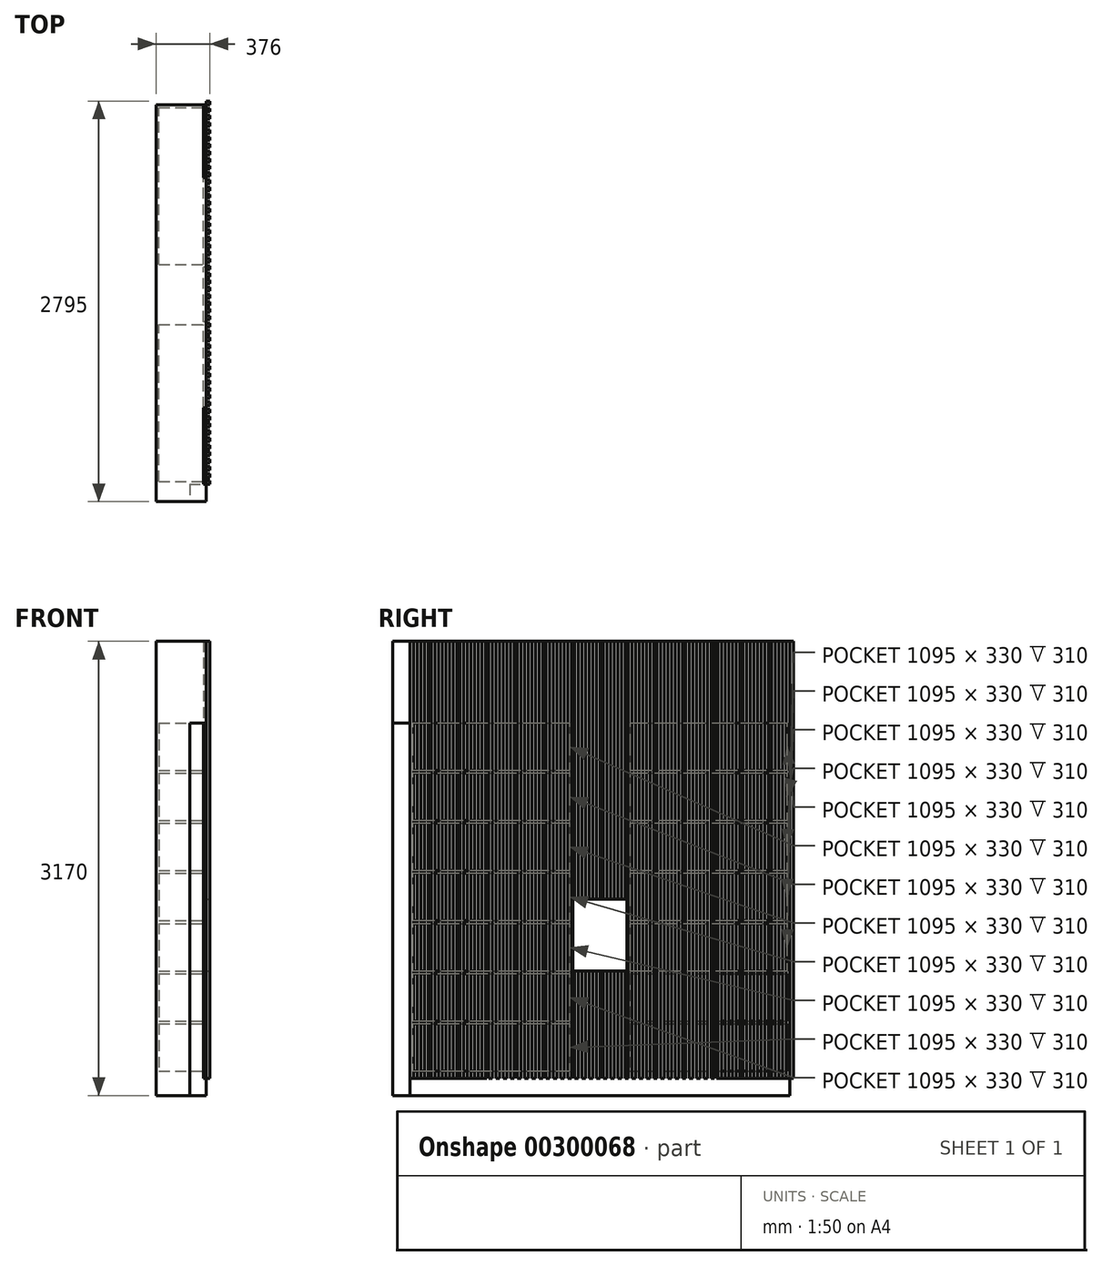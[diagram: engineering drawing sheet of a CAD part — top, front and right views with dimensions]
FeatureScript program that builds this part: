
annotation { "Feature Type Name" : "Feature", "Feature Type Description" : "" }
export const myFeature = defineFeature(function(context is Context, id is Id, definition is map)
    precondition{}
    {
        {
            var Q0;
            Q0=qCreatedBy(makeId("Top.planeOp"),FACE);
            var sketch = newSketch(context, id + "F0", { "sketchPlane" : qUnion([Q0])});
            skLineSegment(sketch, "E0.bottom", {"start": v(0, 0) * mm, "end": v(350, 0) * mm});
            skLineSegment(sketch, "E0.top", {"start": v(0, 2650) * mm, "end": v(350, 2650) * mm});
            skLineSegment(sketch, "E0.left", {"start": v(0, 0) * mm, "end": v(0, 2650) * mm});
            skLineSegment(sketch, "E0.right", {"start": v(350, 0) * mm, "end": v(350, 2650) * mm});
            skLineSegment(sketch, "E1", {"start": v(0, 2770) * mm, "end": v(350, 2770) * mm, "construction": true});
            skSolve(sketch);
        }
        {
            var Q0;
            Q0=qCreatedBy(makeId("Top.planeOp"),FACE);
            cPlane(context, id + "F1", {"entities" : qUnion([Q0]), "cplaneType" : CPlaneType.OFFSET, "offset" : 120 * mm, "width" : 150 * mm, "height" : 150 * mm});
        }
        {
            var Q0;
            Q0=makeQuery(id+"F0.imprint","IMPRINT",FACE,{"disambiguationData":[TD([[makeQuery(id+"F0.imprint","IMPRINT",EDGE,{"derivedFrom":sQuery(id+"F0.wireOp",EDGE,"E0.bottom")}),1.0]])]});
            extrude(context, id + "F2", {"entities" : qUnion([Q0]), "depth" : 3170 * mm});
        }
        {
            var Q0;
            Q0=makeQuery(id+"F2.opExtrude","SWEPT_FACE",FACE,{"disambiguationData":[OSD([sQuery(id+"F0.wireOp",EDGE,"E0.right")])]});
            var sketch = newSketch(context, id + "F3", { "sketchPlane" : qUnion([Q0])});
            skLineSegment(sketch, "E2.bottom", {"start": v(1135, 1370) * mm, "end": v(1515, 1370) * mm});
            skLineSegment(sketch, "E2.top", {"start": v(1135, 870) * mm, "end": v(1515, 870) * mm});
            skLineSegment(sketch, "E2.left", {"start": v(1135, 1370) * mm, "end": v(1135, 870) * mm});
            skLineSegment(sketch, "E2.right", {"start": v(1515, 1370) * mm, "end": v(1515, 870) * mm});
            skLineSegment(sketch, "E3", {"start": v(1135, 1370) * mm, "end": v(1515, 870) * mm, "construction": true});
            skLineSegment(sketch, "E4", {"start": v(1515, 1370) * mm, "end": v(1135, 870) * mm, "construction": true});
            skLineSegment(sketch, "E5", {"start": v(1325, 1120) * mm, "end": v(856.73, 1120) * mm, "construction": true});
            skPoint(sketch, "E5.endSnap0", {"position": v(1135, 1120) * mm});
            skSolve(sketch);
        }
        {
            var Q0;
            Q0=qCreatedBy(makeId("Top.planeOp"),FACE);
            cPlane(context, id + "F4", {"entities" : qUnion([Q0]), "cplaneType" : CPlaneType.OFFSET, "offset" : 3170 * mm, "width" : 150 * mm, "height" : 150 * mm});
        }
        {
            var Q0;
            Q0=qCreatedBy(id+"F1.planeOp",FACE);
            var sketch = newSketch(context, id + "F5", { "sketchPlane" : qUnion([Q0])});
            skLineSegment(sketch, "E6.bottom", {"start": v(351, 0) * mm, "end": v(376, 0) * mm});
            skLineSegment(sketch, "E6.top", {"start": v(351, 25) * mm, "end": v(376, 25) * mm});
            skLineSegment(sketch, "E6.left", {"start": v(351, 0) * mm, "end": v(351, 25) * mm});
            skLineSegment(sketch, "E6.right", {"start": v(376, 0) * mm, "end": v(376, 25) * mm});
            skLineSegment(sketch, "E7.0.1.0", {"start": v(351, 75) * mm, "end": v(376, 75) * mm});
            skLineSegment(sketch, "E7.0.1.1", {"start": v(351, 50) * mm, "end": v(376, 50) * mm});
            skLineSegment(sketch, "E7.0.1.2", {"start": v(376, 50) * mm, "end": v(376, 75) * mm});
            skLineSegment(sketch, "E7.0.1.3", {"start": v(351, 50) * mm, "end": v(351, 75) * mm});
            skLineSegment(sketch, "E7.0.2.0", {"start": v(351, 125) * mm, "end": v(376, 125) * mm});
            skLineSegment(sketch, "E7.0.2.1", {"start": v(351, 100) * mm, "end": v(376, 100) * mm});
            skLineSegment(sketch, "E7.0.2.2", {"start": v(376, 100) * mm, "end": v(376, 125) * mm});
            skLineSegment(sketch, "E7.0.2.3", {"start": v(351, 100) * mm, "end": v(351, 125) * mm});
            skLineSegment(sketch, "E7.0.3.0", {"start": v(351, 175) * mm, "end": v(376, 175) * mm});
            skLineSegment(sketch, "E7.0.3.1", {"start": v(351, 150) * mm, "end": v(376, 150) * mm});
            skLineSegment(sketch, "E7.0.3.2", {"start": v(376, 150) * mm, "end": v(376, 175) * mm});
            skLineSegment(sketch, "E7.0.3.3", {"start": v(351, 150) * mm, "end": v(351, 175) * mm});
            skLineSegment(sketch, "E7.0.4.0", {"start": v(351, 225) * mm, "end": v(376, 225) * mm});
            skLineSegment(sketch, "E7.0.4.1", {"start": v(351, 200) * mm, "end": v(376, 200) * mm});
            skLineSegment(sketch, "E7.0.4.2", {"start": v(376, 200) * mm, "end": v(376, 225) * mm});
            skLineSegment(sketch, "E7.0.4.3", {"start": v(351, 200) * mm, "end": v(351, 225) * mm});
            skLineSegment(sketch, "E7.0.5.0", {"start": v(351, 275) * mm, "end": v(376, 275) * mm});
            skLineSegment(sketch, "E7.0.5.1", {"start": v(351, 250) * mm, "end": v(376, 250) * mm});
            skLineSegment(sketch, "E7.0.5.2", {"start": v(376, 250) * mm, "end": v(376, 275) * mm});
            skLineSegment(sketch, "E7.0.5.3", {"start": v(351, 250) * mm, "end": v(351, 275) * mm});
            skLineSegment(sketch, "E7.0.6.0", {"start": v(351, 325) * mm, "end": v(376, 325) * mm});
            skLineSegment(sketch, "E7.0.6.1", {"start": v(351, 300) * mm, "end": v(376, 300) * mm});
            skLineSegment(sketch, "E7.0.6.2", {"start": v(376, 300) * mm, "end": v(376, 325) * mm});
            skLineSegment(sketch, "E7.0.6.3", {"start": v(351, 300) * mm, "end": v(351, 325) * mm});
            skLineSegment(sketch, "E7.0.7.0", {"start": v(351, 375) * mm, "end": v(376, 375) * mm});
            skLineSegment(sketch, "E7.0.7.1", {"start": v(351, 350) * mm, "end": v(376, 350) * mm});
            skLineSegment(sketch, "E7.0.7.2", {"start": v(376, 350) * mm, "end": v(376, 375) * mm});
            skLineSegment(sketch, "E7.0.7.3", {"start": v(351, 350) * mm, "end": v(351, 375) * mm});
            skLineSegment(sketch, "E7.0.8.0", {"start": v(351, 425) * mm, "end": v(376, 425) * mm});
            skLineSegment(sketch, "E7.0.8.1", {"start": v(351, 400) * mm, "end": v(376, 400) * mm});
            skLineSegment(sketch, "E7.0.8.2", {"start": v(376, 400) * mm, "end": v(376, 425) * mm});
            skLineSegment(sketch, "E7.0.8.3", {"start": v(351, 400) * mm, "end": v(351, 425) * mm});
            skLineSegment(sketch, "E7.0.9.0", {"start": v(351, 475) * mm, "end": v(376, 475) * mm});
            skLineSegment(sketch, "E7.0.9.1", {"start": v(351, 450) * mm, "end": v(376, 450) * mm});
            skLineSegment(sketch, "E7.0.9.2", {"start": v(376, 450) * mm, "end": v(376, 475) * mm});
            skLineSegment(sketch, "E7.0.9.3", {"start": v(351, 450) * mm, "end": v(351, 475) * mm});
            skLineSegment(sketch, "E7.0.10.0", {"start": v(351, 525) * mm, "end": v(376, 525) * mm});
            skLineSegment(sketch, "E7.0.10.1", {"start": v(351, 500) * mm, "end": v(376, 500) * mm});
            skLineSegment(sketch, "E7.0.10.2", {"start": v(376, 500) * mm, "end": v(376, 525) * mm});
            skLineSegment(sketch, "E7.0.10.3", {"start": v(351, 500) * mm, "end": v(351, 525) * mm});
            skLineSegment(sketch, "E7.0.11.0", {"start": v(351, 575) * mm, "end": v(376, 575) * mm});
            skLineSegment(sketch, "E7.0.11.1", {"start": v(351, 550) * mm, "end": v(376, 550) * mm});
            skLineSegment(sketch, "E7.0.11.2", {"start": v(376, 550) * mm, "end": v(376, 575) * mm});
            skLineSegment(sketch, "E7.0.11.3", {"start": v(351, 550) * mm, "end": v(351, 575) * mm});
            skLineSegment(sketch, "E7.0.12.0", {"start": v(351, 625) * mm, "end": v(376, 625) * mm});
            skLineSegment(sketch, "E7.0.12.1", {"start": v(351, 600) * mm, "end": v(376, 600) * mm});
            skLineSegment(sketch, "E7.0.12.2", {"start": v(376, 600) * mm, "end": v(376, 625) * mm});
            skLineSegment(sketch, "E7.0.12.3", {"start": v(351, 600) * mm, "end": v(351, 625) * mm});
            skLineSegment(sketch, "E7.0.13.0", {"start": v(351, 675) * mm, "end": v(376, 675) * mm});
            skLineSegment(sketch, "E7.0.13.1", {"start": v(351, 650) * mm, "end": v(376, 650) * mm});
            skLineSegment(sketch, "E7.0.13.2", {"start": v(376, 650) * mm, "end": v(376, 675) * mm});
            skLineSegment(sketch, "E7.0.13.3", {"start": v(351, 650) * mm, "end": v(351, 675) * mm});
            skLineSegment(sketch, "E7.0.14.0", {"start": v(351, 725) * mm, "end": v(376, 725) * mm});
            skLineSegment(sketch, "E7.0.14.1", {"start": v(351, 700) * mm, "end": v(376, 700) * mm});
            skLineSegment(sketch, "E7.0.14.2", {"start": v(376, 700) * mm, "end": v(376, 725) * mm});
            skLineSegment(sketch, "E7.0.14.3", {"start": v(351, 700) * mm, "end": v(351, 725) * mm});
            skLineSegment(sketch, "E7.0.15.0", {"start": v(351, 775) * mm, "end": v(376, 775) * mm});
            skLineSegment(sketch, "E7.0.15.1", {"start": v(351, 750) * mm, "end": v(376, 750) * mm});
            skLineSegment(sketch, "E7.0.15.2", {"start": v(376, 750) * mm, "end": v(376, 775) * mm});
            skLineSegment(sketch, "E7.0.15.3", {"start": v(351, 750) * mm, "end": v(351, 775) * mm});
            skLineSegment(sketch, "E7.0.16.0", {"start": v(351, 825) * mm, "end": v(376, 825) * mm});
            skLineSegment(sketch, "E7.0.16.1", {"start": v(351, 800) * mm, "end": v(376, 800) * mm});
            skLineSegment(sketch, "E7.0.16.2", {"start": v(376, 800) * mm, "end": v(376, 825) * mm});
            skLineSegment(sketch, "E7.0.16.3", {"start": v(351, 800) * mm, "end": v(351, 825) * mm});
            skLineSegment(sketch, "E7.0.17.0", {"start": v(351, 875) * mm, "end": v(376, 875) * mm});
            skLineSegment(sketch, "E7.0.17.1", {"start": v(351, 850) * mm, "end": v(376, 850) * mm});
            skLineSegment(sketch, "E7.0.17.2", {"start": v(376, 850) * mm, "end": v(376, 875) * mm});
            skLineSegment(sketch, "E7.0.17.3", {"start": v(351, 850) * mm, "end": v(351, 875) * mm});
            skLineSegment(sketch, "E7.0.18.0", {"start": v(351, 925) * mm, "end": v(376, 925) * mm});
            skLineSegment(sketch, "E7.0.18.1", {"start": v(351, 900) * mm, "end": v(376, 900) * mm});
            skLineSegment(sketch, "E7.0.18.2", {"start": v(376, 900) * mm, "end": v(376, 925) * mm});
            skLineSegment(sketch, "E7.0.18.3", {"start": v(351, 900) * mm, "end": v(351, 925) * mm});
            skLineSegment(sketch, "E7.0.19.0", {"start": v(351, 975) * mm, "end": v(376, 975) * mm});
            skLineSegment(sketch, "E7.0.19.1", {"start": v(351, 950) * mm, "end": v(376, 950) * mm});
            skLineSegment(sketch, "E7.0.19.2", {"start": v(376, 950) * mm, "end": v(376, 975) * mm});
            skLineSegment(sketch, "E7.0.19.3", {"start": v(351, 950) * mm, "end": v(351, 975) * mm});
            skLineSegment(sketch, "E7.0.20.0", {"start": v(351, 1025) * mm, "end": v(376, 1025) * mm});
            skLineSegment(sketch, "E7.0.20.1", {"start": v(351, 1000) * mm, "end": v(376, 1000) * mm});
            skLineSegment(sketch, "E7.0.20.2", {"start": v(376, 1000) * mm, "end": v(376, 1025) * mm});
            skLineSegment(sketch, "E7.0.20.3", {"start": v(351, 1000) * mm, "end": v(351, 1025) * mm});
            skLineSegment(sketch, "E7.0.21.0", {"start": v(351, 1075) * mm, "end": v(376, 1075) * mm});
            skLineSegment(sketch, "E7.0.21.1", {"start": v(351, 1050) * mm, "end": v(376, 1050) * mm});
            skLineSegment(sketch, "E7.0.21.2", {"start": v(376, 1050) * mm, "end": v(376, 1075) * mm});
            skLineSegment(sketch, "E7.0.21.3", {"start": v(351, 1050) * mm, "end": v(351, 1075) * mm});
            skLineSegment(sketch, "E7.direction1", {"start": v(351, 0) * mm, "end": v(376, 0) * mm, "construction": true});
            skLineSegment(sketch, "E7.direction2", {"start": v(351, 0) * mm, "end": v(351, 50) * mm, "construction": true});
            skLineSegment(sketch, "E8.0.0.22", {"start": v(351, 1125) * mm, "end": v(376, 1125) * mm});
            skLineSegment(sketch, "E8.3.0.22", {"start": v(351, 1100) * mm, "end": v(376, 1100) * mm});
            skLineSegment(sketch, "E8.6.0.22", {"start": v(376, 1100) * mm, "end": v(376, 1125) * mm});
            skLineSegment(sketch, "E8.9.0.22", {"start": v(351, 1100) * mm, "end": v(351, 1125) * mm});
            skLineSegment(sketch, "E8.0.0.23", {"start": v(351, 1175) * mm, "end": v(376, 1175) * mm});
            skLineSegment(sketch, "E8.3.0.23", {"start": v(351, 1150) * mm, "end": v(376, 1150) * mm});
            skLineSegment(sketch, "E8.6.0.23", {"start": v(376, 1150) * mm, "end": v(376, 1175) * mm});
            skLineSegment(sketch, "E8.9.0.23", {"start": v(351, 1150) * mm, "end": v(351, 1175) * mm});
            skLineSegment(sketch, "E8.0.0.24", {"start": v(351, 1225) * mm, "end": v(376, 1225) * mm});
            skLineSegment(sketch, "E8.3.0.24", {"start": v(351, 1200) * mm, "end": v(376, 1200) * mm});
            skLineSegment(sketch, "E8.6.0.24", {"start": v(376, 1200) * mm, "end": v(376, 1225) * mm});
            skLineSegment(sketch, "E8.9.0.24", {"start": v(351, 1200) * mm, "end": v(351, 1225) * mm});
            skLineSegment(sketch, "E9.0.0.25", {"start": v(351, 1275) * mm, "end": v(376, 1275) * mm});
            skLineSegment(sketch, "E9.3.0.25", {"start": v(351, 1250) * mm, "end": v(376, 1250) * mm});
            skLineSegment(sketch, "E9.6.0.25", {"start": v(376, 1250) * mm, "end": v(376, 1275) * mm});
            skLineSegment(sketch, "E9.9.0.25", {"start": v(351, 1250) * mm, "end": v(351, 1275) * mm});
            skLineSegment(sketch, "E9.0.0.26", {"start": v(351, 1325) * mm, "end": v(376, 1325) * mm});
            skLineSegment(sketch, "E9.3.0.26", {"start": v(351, 1300) * mm, "end": v(376, 1300) * mm});
            skLineSegment(sketch, "E9.6.0.26", {"start": v(376, 1300) * mm, "end": v(376, 1325) * mm});
            skLineSegment(sketch, "E9.9.0.26", {"start": v(351, 1300) * mm, "end": v(351, 1325) * mm});
            skLineSegment(sketch, "E9.0.0.27", {"start": v(351, 1375) * mm, "end": v(376, 1375) * mm});
            skLineSegment(sketch, "E9.3.0.27", {"start": v(351, 1350) * mm, "end": v(376, 1350) * mm});
            skLineSegment(sketch, "E9.6.0.27", {"start": v(376, 1350) * mm, "end": v(376, 1375) * mm});
            skLineSegment(sketch, "E9.9.0.27", {"start": v(351, 1350) * mm, "end": v(351, 1375) * mm});
            skLineSegment(sketch, "E9.0.0.28", {"start": v(351, 1425) * mm, "end": v(376, 1425) * mm});
            skLineSegment(sketch, "E9.3.0.28", {"start": v(351, 1400) * mm, "end": v(376, 1400) * mm});
            skLineSegment(sketch, "E9.6.0.28", {"start": v(376, 1400) * mm, "end": v(376, 1425) * mm});
            skLineSegment(sketch, "E9.9.0.28", {"start": v(351, 1400) * mm, "end": v(351, 1425) * mm});
            skLineSegment(sketch, "E9.0.0.29", {"start": v(351, 1475) * mm, "end": v(376, 1475) * mm});
            skLineSegment(sketch, "E9.3.0.29", {"start": v(351, 1450) * mm, "end": v(376, 1450) * mm});
            skLineSegment(sketch, "E9.6.0.29", {"start": v(376, 1450) * mm, "end": v(376, 1475) * mm});
            skLineSegment(sketch, "E9.9.0.29", {"start": v(351, 1450) * mm, "end": v(351, 1475) * mm});
            skLineSegment(sketch, "E9.0.0.30", {"start": v(351, 1525) * mm, "end": v(376, 1525) * mm});
            skLineSegment(sketch, "E9.3.0.30", {"start": v(351, 1500) * mm, "end": v(376, 1500) * mm});
            skLineSegment(sketch, "E9.6.0.30", {"start": v(376, 1500) * mm, "end": v(376, 1525) * mm});
            skLineSegment(sketch, "E9.9.0.30", {"start": v(351, 1500) * mm, "end": v(351, 1525) * mm});
            skLineSegment(sketch, "E9.0.0.31", {"start": v(351, 1575) * mm, "end": v(376, 1575) * mm});
            skLineSegment(sketch, "E9.3.0.31", {"start": v(351, 1550) * mm, "end": v(376, 1550) * mm});
            skLineSegment(sketch, "E9.6.0.31", {"start": v(376, 1550) * mm, "end": v(376, 1575) * mm});
            skLineSegment(sketch, "E9.9.0.31", {"start": v(351, 1550) * mm, "end": v(351, 1575) * mm});
            skLineSegment(sketch, "E9.0.0.32", {"start": v(351, 1625) * mm, "end": v(376, 1625) * mm});
            skLineSegment(sketch, "E9.3.0.32", {"start": v(351, 1600) * mm, "end": v(376, 1600) * mm});
            skLineSegment(sketch, "E9.6.0.32", {"start": v(376, 1600) * mm, "end": v(376, 1625) * mm});
            skLineSegment(sketch, "E9.9.0.32", {"start": v(351, 1600) * mm, "end": v(351, 1625) * mm});
            skLineSegment(sketch, "E9.0.0.33", {"start": v(351, 1675) * mm, "end": v(376, 1675) * mm});
            skLineSegment(sketch, "E9.3.0.33", {"start": v(351, 1650) * mm, "end": v(376, 1650) * mm});
            skLineSegment(sketch, "E9.6.0.33", {"start": v(376, 1650) * mm, "end": v(376, 1675) * mm});
            skLineSegment(sketch, "E9.9.0.33", {"start": v(351, 1650) * mm, "end": v(351, 1675) * mm});
            skLineSegment(sketch, "E9.0.0.34", {"start": v(351, 1725) * mm, "end": v(376, 1725) * mm});
            skLineSegment(sketch, "E9.3.0.34", {"start": v(351, 1700) * mm, "end": v(376, 1700) * mm});
            skLineSegment(sketch, "E9.6.0.34", {"start": v(376, 1700) * mm, "end": v(376, 1725) * mm});
            skLineSegment(sketch, "E9.9.0.34", {"start": v(351, 1700) * mm, "end": v(351, 1725) * mm});
            skLineSegment(sketch, "E9.0.0.35", {"start": v(351, 1775) * mm, "end": v(376, 1775) * mm});
            skLineSegment(sketch, "E9.3.0.35", {"start": v(351, 1750) * mm, "end": v(376, 1750) * mm});
            skLineSegment(sketch, "E9.6.0.35", {"start": v(376, 1750) * mm, "end": v(376, 1775) * mm});
            skLineSegment(sketch, "E9.9.0.35", {"start": v(351, 1750) * mm, "end": v(351, 1775) * mm});
            skLineSegment(sketch, "E9.0.0.36", {"start": v(351, 1825) * mm, "end": v(376, 1825) * mm});
            skLineSegment(sketch, "E9.3.0.36", {"start": v(351, 1800) * mm, "end": v(376, 1800) * mm});
            skLineSegment(sketch, "E9.6.0.36", {"start": v(376, 1800) * mm, "end": v(376, 1825) * mm});
            skLineSegment(sketch, "E9.9.0.36", {"start": v(351, 1800) * mm, "end": v(351, 1825) * mm});
            skLineSegment(sketch, "E9.0.0.37", {"start": v(351, 1875) * mm, "end": v(376, 1875) * mm});
            skLineSegment(sketch, "E9.3.0.37", {"start": v(351, 1850) * mm, "end": v(376, 1850) * mm});
            skLineSegment(sketch, "E9.6.0.37", {"start": v(376, 1850) * mm, "end": v(376, 1875) * mm});
            skLineSegment(sketch, "E9.9.0.37", {"start": v(351, 1850) * mm, "end": v(351, 1875) * mm});
            skLineSegment(sketch, "E9.0.0.38", {"start": v(351, 1925) * mm, "end": v(376, 1925) * mm});
            skLineSegment(sketch, "E9.3.0.38", {"start": v(351, 1900) * mm, "end": v(376, 1900) * mm});
            skLineSegment(sketch, "E9.6.0.38", {"start": v(376, 1900) * mm, "end": v(376, 1925) * mm});
            skLineSegment(sketch, "E9.9.0.38", {"start": v(351, 1900) * mm, "end": v(351, 1925) * mm});
            skLineSegment(sketch, "E9.0.0.39", {"start": v(351, 1975) * mm, "end": v(376, 1975) * mm});
            skLineSegment(sketch, "E9.3.0.39", {"start": v(351, 1950) * mm, "end": v(376, 1950) * mm});
            skLineSegment(sketch, "E9.6.0.39", {"start": v(376, 1950) * mm, "end": v(376, 1975) * mm});
            skLineSegment(sketch, "E9.9.0.39", {"start": v(351, 1950) * mm, "end": v(351, 1975) * mm});
            skLineSegment(sketch, "E9.0.0.40", {"start": v(351, 2025) * mm, "end": v(376, 2025) * mm});
            skLineSegment(sketch, "E9.3.0.40", {"start": v(351, 2000) * mm, "end": v(376, 2000) * mm});
            skLineSegment(sketch, "E9.6.0.40", {"start": v(376, 2000) * mm, "end": v(376, 2025) * mm});
            skLineSegment(sketch, "E9.9.0.40", {"start": v(351, 2000) * mm, "end": v(351, 2025) * mm});
            skLineSegment(sketch, "E9.0.0.41", {"start": v(351, 2075) * mm, "end": v(376, 2075) * mm});
            skLineSegment(sketch, "E9.3.0.41", {"start": v(351, 2050) * mm, "end": v(376, 2050) * mm});
            skLineSegment(sketch, "E9.6.0.41", {"start": v(376, 2050) * mm, "end": v(376, 2075) * mm});
            skLineSegment(sketch, "E9.9.0.41", {"start": v(351, 2050) * mm, "end": v(351, 2075) * mm});
            skLineSegment(sketch, "E9.0.0.42", {"start": v(351, 2125) * mm, "end": v(376, 2125) * mm});
            skLineSegment(sketch, "E9.3.0.42", {"start": v(351, 2100) * mm, "end": v(376, 2100) * mm});
            skLineSegment(sketch, "E9.6.0.42", {"start": v(376, 2100) * mm, "end": v(376, 2125) * mm});
            skLineSegment(sketch, "E9.9.0.42", {"start": v(351, 2100) * mm, "end": v(351, 2125) * mm});
            skLineSegment(sketch, "E9.0.0.43", {"start": v(351, 2175) * mm, "end": v(376, 2175) * mm});
            skLineSegment(sketch, "E9.3.0.43", {"start": v(351, 2150) * mm, "end": v(376, 2150) * mm});
            skLineSegment(sketch, "E9.6.0.43", {"start": v(376, 2150) * mm, "end": v(376, 2175) * mm});
            skLineSegment(sketch, "E9.9.0.43", {"start": v(351, 2150) * mm, "end": v(351, 2175) * mm});
            skLineSegment(sketch, "E9.0.0.44", {"start": v(351, 2225) * mm, "end": v(376, 2225) * mm});
            skLineSegment(sketch, "E9.3.0.44", {"start": v(351, 2200) * mm, "end": v(376, 2200) * mm});
            skLineSegment(sketch, "E9.6.0.44", {"start": v(376, 2200) * mm, "end": v(376, 2225) * mm});
            skLineSegment(sketch, "E9.9.0.44", {"start": v(351, 2200) * mm, "end": v(351, 2225) * mm});
            skLineSegment(sketch, "E9.0.0.45", {"start": v(351, 2275) * mm, "end": v(376, 2275) * mm});
            skLineSegment(sketch, "E9.3.0.45", {"start": v(351, 2250) * mm, "end": v(376, 2250) * mm});
            skLineSegment(sketch, "E9.6.0.45", {"start": v(376, 2250) * mm, "end": v(376, 2275) * mm});
            skLineSegment(sketch, "E9.9.0.45", {"start": v(351, 2250) * mm, "end": v(351, 2275) * mm});
            skLineSegment(sketch, "E9.0.0.46", {"start": v(351, 2325) * mm, "end": v(376, 2325) * mm});
            skLineSegment(sketch, "E9.3.0.46", {"start": v(351, 2300) * mm, "end": v(376, 2300) * mm});
            skLineSegment(sketch, "E9.6.0.46", {"start": v(376, 2300) * mm, "end": v(376, 2325) * mm});
            skLineSegment(sketch, "E9.9.0.46", {"start": v(351, 2300) * mm, "end": v(351, 2325) * mm});
            skLineSegment(sketch, "E9.0.0.47", {"start": v(351, 2375) * mm, "end": v(376, 2375) * mm});
            skLineSegment(sketch, "E9.3.0.47", {"start": v(351, 2350) * mm, "end": v(376, 2350) * mm});
            skLineSegment(sketch, "E9.6.0.47", {"start": v(376, 2350) * mm, "end": v(376, 2375) * mm});
            skLineSegment(sketch, "E9.9.0.47", {"start": v(351, 2350) * mm, "end": v(351, 2375) * mm});
            skLineSegment(sketch, "E9.0.0.48", {"start": v(351, 2425) * mm, "end": v(376, 2425) * mm});
            skLineSegment(sketch, "E9.3.0.48", {"start": v(351, 2400) * mm, "end": v(376, 2400) * mm});
            skLineSegment(sketch, "E9.6.0.48", {"start": v(376, 2400) * mm, "end": v(376, 2425) * mm});
            skLineSegment(sketch, "E9.9.0.48", {"start": v(351, 2400) * mm, "end": v(351, 2425) * mm});
            skLineSegment(sketch, "E9.0.0.49", {"start": v(351, 2475) * mm, "end": v(376, 2475) * mm});
            skLineSegment(sketch, "E9.3.0.49", {"start": v(351, 2450) * mm, "end": v(376, 2450) * mm});
            skLineSegment(sketch, "E9.6.0.49", {"start": v(376, 2450) * mm, "end": v(376, 2475) * mm});
            skLineSegment(sketch, "E9.9.0.49", {"start": v(351, 2450) * mm, "end": v(351, 2475) * mm});
            skLineSegment(sketch, "E10.0.0.50", {"start": v(351, 2525) * mm, "end": v(376, 2525) * mm});
            skLineSegment(sketch, "E10.3.0.50", {"start": v(351, 2500) * mm, "end": v(376, 2500) * mm});
            skLineSegment(sketch, "E10.6.0.50", {"start": v(376, 2500) * mm, "end": v(376, 2525) * mm});
            skLineSegment(sketch, "E10.9.0.50", {"start": v(351, 2500) * mm, "end": v(351, 2525) * mm});
            skLineSegment(sketch, "E10.0.0.51", {"start": v(351, 2575) * mm, "end": v(376, 2575) * mm});
            skLineSegment(sketch, "E10.3.0.51", {"start": v(351, 2550) * mm, "end": v(376, 2550) * mm});
            skLineSegment(sketch, "E10.6.0.51", {"start": v(376, 2550) * mm, "end": v(376, 2575) * mm});
            skLineSegment(sketch, "E10.9.0.51", {"start": v(351, 2550) * mm, "end": v(351, 2575) * mm});
            skLineSegment(sketch, "E10.0.0.52", {"start": v(351, 2625) * mm, "end": v(376, 2625) * mm});
            skLineSegment(sketch, "E10.3.0.52", {"start": v(351, 2600) * mm, "end": v(376, 2600) * mm});
            skLineSegment(sketch, "E10.6.0.52", {"start": v(376, 2600) * mm, "end": v(376, 2625) * mm});
            skLineSegment(sketch, "E10.9.0.52", {"start": v(351, 2600) * mm, "end": v(351, 2625) * mm});
            skLineSegment(sketch, "E10.0.0.53", {"start": v(351, 2675) * mm, "end": v(376, 2675) * mm});
            skLineSegment(sketch, "E10.3.0.53", {"start": v(351, 2650) * mm, "end": v(376, 2650) * mm});
            skLineSegment(sketch, "E10.6.0.53", {"start": v(376, 2650) * mm, "end": v(376, 2675) * mm});
            skLineSegment(sketch, "E10.9.0.53", {"start": v(351, 2650) * mm, "end": v(351, 2675) * mm});
            skSolve(sketch);
        }
        {
            var Q0;
            Q0=qSketchRegion(id+"F5",true);
            var Q1;
            Q1=qCreatedBy(id+"F4.planeOp",FACE);
            extrude(context, id + "F6", {"entities" : qUnion([Q0]), "endBound" : BoundingType.UP_TO_SURFACE, "endBoundEntityFace" : qUnion([Q1]), "depth" : 2525 * mm});
        }
        {
            var Q0;
            Q0 = qSketchRegion(id + "F3", true);
            extrude(context, id + "F7", {"entities" : qUnion([Q0]), "operationType" : NewBodyOperationType.REMOVE, "endBound" : BoundingType.THROUGH_ALL, "depth" : 25 * mm, "hasSecondDirection" : true, "secondDirectionOppositeDirection" : true, "secondDirectionDepth" : 20 * mm});
        }
        {
            var Q0;
            Q0=makeQuery(id+"F3.imprint","IMPRINT",FACE,{"disambiguationData":[TD([[makeQuery(id+"F3.imprint","IMPRINT",EDGE,{"derivedFrom":sQuery(id+"F3.wireOp",EDGE,"E2.bottom")}),1.0]])]});
            var sketch = newSketch(context, id + "F8", { "sketchPlane" : qUnion([Q0])});
            skLineSegment(sketch, "E11.bottom", {"start": v(2140, 3170) * mm, "end": v(2650, 3170) * mm});
            skLineSegment(sketch, "E11.top", {"start": v(2140, 120) * mm, "end": v(2650, 120) * mm});
            skLineSegment(sketch, "E11.left", {"start": v(2140, 3170) * mm, "end": v(2140, 120) * mm});
            skLineSegment(sketch, "E11.right", {"start": v(2650, 3170) * mm, "end": v(2650, 120) * mm});
            skLineSegment(sketch, "E12.bottom", {"start": v(0, 3170) * mm, "end": v(535, 3170) * mm});
            skLineSegment(sketch, "E12.top", {"start": v(0, 120) * mm, "end": v(535, 120) * mm});
            skLineSegment(sketch, "E12.left", {"start": v(0, 3170) * mm, "end": v(0, 120) * mm});
            skLineSegment(sketch, "E12.right", {"start": v(535, 3170) * mm, "end": v(535, 120) * mm});
            skSolve(sketch);
        }
        {
            var Q0;
            Q0 = qSketchRegion(id + "F8", true);
            extrude(context, id + "F9", {"entities" : qUnion([Q0]), "operationType" : NewBodyOperationType.REMOVE, "oppositeDirection" : true, "depth" : 20 * mm});
        }
        {
            var Q0;
            Q0=makeQuery(id+"F2.opExtrude","SWEPT_FACE",FACE,{"disambiguationData":[OSD([sQuery(id+"F0.wireOp",EDGE,"E0.left")])]});
            cPlane(context, id + "F10", {"entities" : qUnion([Q0]), "cplaneType" : CPlaneType.OFFSET, "offset" : 20 * mm, "oppositeDirection" : true, "width" : 150 * mm, "height" : 150 * mm});
        }
        {
            var Q0;
            Q0=makeQuery(id+"F9.boolean.opBoolean","COPY",FACE,{"derivedFrom":makeQuery(id+"F9.opExtrude","CAP_FACE",FACE,{"disambiguationData":[OSD([sQuery(id+"F8.wireOp",EDGE,"E12.bottom"),sQuery(id+"F8.wireOp",EDGE,"E12.top"),sQuery(id+"F8.wireOp",EDGE,"E12.left"),sQuery(id+"F8.wireOp",EDGE,"E12.right")])],"isStart":false})});
            var sketch = newSketch(context, id + "F11", { "sketchPlane" : qUnion([Q0])});
            skLineSegment(sketch, "E13.bottom", {"start": v(20, 500) * mm, "end": v(1115, 500) * mm});
            skLineSegment(sketch, "E13.top", {"start": v(20, 170) * mm, "end": v(1115, 170) * mm});
            skLineSegment(sketch, "E13.left", {"start": v(20, 500) * mm, "end": v(20, 170) * mm});
            skLineSegment(sketch, "E13.right", {"start": v(1115, 500) * mm, "end": v(1115, 170) * mm});
            skLineSegment(sketch, "E14.bottom", {"start": v(1535, 500) * mm, "end": v(2630, 500) * mm});
            skLineSegment(sketch, "E14.top", {"start": v(1535, 170) * mm, "end": v(2630, 170) * mm});
            skLineSegment(sketch, "E14.left", {"start": v(1535, 500) * mm, "end": v(1535, 170) * mm});
            skLineSegment(sketch, "E14.right", {"start": v(2630, 500) * mm, "end": v(2630, 170) * mm});
            skLineSegment(sketch, "E15.0.1.0", {"start": v(1115, 850) * mm, "end": v(1115, 520) * mm});
            skLineSegment(sketch, "E15.0.1.1", {"start": v(1535, 850) * mm, "end": v(2630, 850) * mm});
            skLineSegment(sketch, "E15.0.1.2", {"start": v(20, 850) * mm, "end": v(20, 520) * mm});
            skLineSegment(sketch, "E15.0.1.3", {"start": v(20, 850) * mm, "end": v(1115, 850) * mm});
            skLineSegment(sketch, "E15.0.1.4", {"start": v(1535, 850) * mm, "end": v(1535, 520) * mm});
            skLineSegment(sketch, "E15.0.1.5", {"start": v(2630, 850) * mm, "end": v(2630, 520) * mm});
            skLineSegment(sketch, "E15.0.1.6", {"start": v(20, 520) * mm, "end": v(1115, 520) * mm});
            skLineSegment(sketch, "E15.0.1.7", {"start": v(1535, 520) * mm, "end": v(2630, 520) * mm});
            skLineSegment(sketch, "E15.0.2.0", {"start": v(1115, 1200) * mm, "end": v(1115, 870) * mm});
            skLineSegment(sketch, "E15.0.2.1", {"start": v(1535, 1200) * mm, "end": v(2630, 1200) * mm});
            skLineSegment(sketch, "E15.0.2.2", {"start": v(20, 1200) * mm, "end": v(20, 870) * mm});
            skLineSegment(sketch, "E15.0.2.3", {"start": v(20, 1200) * mm, "end": v(1115, 1200) * mm});
            skLineSegment(sketch, "E15.0.2.4", {"start": v(1535, 1200) * mm, "end": v(1535, 870) * mm});
            skLineSegment(sketch, "E15.0.2.5", {"start": v(2630, 1200) * mm, "end": v(2630, 870) * mm});
            skLineSegment(sketch, "E15.0.2.6", {"start": v(20, 870) * mm, "end": v(1115, 870) * mm});
            skLineSegment(sketch, "E15.0.2.7", {"start": v(1535, 870) * mm, "end": v(2630, 870) * mm});
            skLineSegment(sketch, "E15.0.3.0", {"start": v(1115, 1550) * mm, "end": v(1115, 1220) * mm});
            skLineSegment(sketch, "E15.0.3.1", {"start": v(1535, 1550) * mm, "end": v(2630, 1550) * mm});
            skLineSegment(sketch, "E15.0.3.2", {"start": v(20, 1550) * mm, "end": v(20, 1220) * mm});
            skLineSegment(sketch, "E15.0.3.3", {"start": v(20, 1550) * mm, "end": v(1115, 1550) * mm});
            skLineSegment(sketch, "E15.0.3.4", {"start": v(1535, 1550) * mm, "end": v(1535, 1220) * mm});
            skLineSegment(sketch, "E15.0.3.5", {"start": v(2630, 1550) * mm, "end": v(2630, 1220) * mm});
            skLineSegment(sketch, "E15.0.3.6", {"start": v(20, 1220) * mm, "end": v(1115, 1220) * mm});
            skLineSegment(sketch, "E15.0.3.7", {"start": v(1535, 1220) * mm, "end": v(2630, 1220) * mm});
            skLineSegment(sketch, "E15.0.4.0", {"start": v(1115, 1900) * mm, "end": v(1115, 1570) * mm});
            skLineSegment(sketch, "E15.0.4.1", {"start": v(1535, 1900) * mm, "end": v(2630, 1900) * mm});
            skLineSegment(sketch, "E15.0.4.2", {"start": v(20, 1900) * mm, "end": v(20, 1570) * mm});
            skLineSegment(sketch, "E15.0.4.3", {"start": v(20, 1900) * mm, "end": v(1115, 1900) * mm});
            skLineSegment(sketch, "E15.0.4.4", {"start": v(1535, 1900) * mm, "end": v(1535, 1570) * mm});
            skLineSegment(sketch, "E15.0.4.5", {"start": v(2630, 1900) * mm, "end": v(2630, 1570) * mm});
            skLineSegment(sketch, "E15.0.4.6", {"start": v(20, 1570) * mm, "end": v(1115, 1570) * mm});
            skLineSegment(sketch, "E15.0.4.7", {"start": v(1535, 1570) * mm, "end": v(2630, 1570) * mm});
            skLineSegment(sketch, "E15.0.5.0", {"start": v(1115, 2250) * mm, "end": v(1115, 1920) * mm});
            skLineSegment(sketch, "E15.0.5.1", {"start": v(1535, 2250) * mm, "end": v(2630, 2250) * mm});
            skLineSegment(sketch, "E15.0.5.2", {"start": v(20, 2250) * mm, "end": v(20, 1920) * mm});
            skLineSegment(sketch, "E15.0.5.3", {"start": v(20, 2250) * mm, "end": v(1115, 2250) * mm});
            skLineSegment(sketch, "E15.0.5.4", {"start": v(1535, 2250) * mm, "end": v(1535, 1920) * mm});
            skLineSegment(sketch, "E15.0.5.5", {"start": v(2630, 2250) * mm, "end": v(2630, 1920) * mm});
            skLineSegment(sketch, "E15.0.5.6", {"start": v(20, 1920) * mm, "end": v(1115, 1920) * mm});
            skLineSegment(sketch, "E15.0.5.7", {"start": v(1535, 1920) * mm, "end": v(2630, 1920) * mm});
            skLineSegment(sketch, "E15.0.6.0", {"start": v(1115, 2600) * mm, "end": v(1115, 2270) * mm});
            skLineSegment(sketch, "E15.0.6.1", {"start": v(1535, 2600) * mm, "end": v(2630, 2600) * mm});
            skLineSegment(sketch, "E15.0.6.2", {"start": v(20, 2600) * mm, "end": v(20, 2270) * mm});
            skLineSegment(sketch, "E15.0.6.3", {"start": v(20, 2600) * mm, "end": v(1115, 2600) * mm});
            skLineSegment(sketch, "E15.0.6.4", {"start": v(1535, 2600) * mm, "end": v(1535, 2270) * mm});
            skLineSegment(sketch, "E15.0.6.5", {"start": v(2630, 2600) * mm, "end": v(2630, 2270) * mm});
            skLineSegment(sketch, "E15.0.6.6", {"start": v(20, 2270) * mm, "end": v(1115, 2270) * mm});
            skLineSegment(sketch, "E15.0.6.7", {"start": v(1535, 2270) * mm, "end": v(2630, 2270) * mm});
            skLineSegment(sketch, "E15.direction1", {"start": v(20, 170) * mm, "end": v(45, 170) * mm, "construction": true});
            skLineSegment(sketch, "E15.direction2", {"start": v(20, 170) * mm, "end": v(20, 520) * mm, "construction": true});
            skSolve(sketch);
        }
        {
            var Q0;
            Q0 = qSketchRegion(id + "F11", true);
            var Q1;
            Q1=qCreatedBy(id+"F10.planeOp",FACE);
            extrude(context, id + "F12", {"entities" : qUnion([Q0]), "operationType" : NewBodyOperationType.REMOVE, "endBound" : BoundingType.UP_TO_SURFACE, "oppositeDirection" : true, "endBoundEntityFace" : qUnion([Q1]), "depth" : 25 * mm});
        }
        {
            var Q0;
            Q0=qCreatedBy(makeId("Top.planeOp"),FACE);
            var sketch = newSketch(context, id + "F13", { "sketchPlane" : qUnion([Q0])});
            skLineSegment(sketch, "E16.bottom", {"start": v(0, 0) * mm, "end": v(235, 0) * mm});
            skLineSegment(sketch, "E16.top", {"start": v(0, -120) * mm, "end": v(235, -120) * mm});
            skLineSegment(sketch, "E16.left", {"start": v(0, 0) * mm, "end": v(0, -120) * mm});
            skLineSegment(sketch, "E16.right", {"start": v(235, 0) * mm, "end": v(235, -120) * mm});
            skSolve(sketch);
        }
        {
            var Q0;
            Q0 = qSketchRegion(id + "F13", true);
            var Q1;
            Q1=makeQuery(id+"F2.opExtrude","CAP_FACE",FACE,{"disambiguationData":[OSD([sQuery(id+"F0.wireOp",EDGE,"E0.bottom"),sQuery(id+"F0.wireOp",EDGE,"E0.top"),sQuery(id+"F0.wireOp",EDGE,"E0.left"),sQuery(id+"F0.wireOp",EDGE,"E0.right")])],"isStart":false});
            extrude(context, id + "F14", {"entities" : qUnion([Q0]), "operationType" : NewBodyOperationType.ADD, "endBound" : BoundingType.UP_TO_SURFACE, "endBoundEntityFace" : qUnion([Q1]), "depth" : 25 * mm});
        }
        {
            var Q0;
            Q0=qCreatedBy(id+"F4.planeOp",FACE);
            var sketch = newSketch(context, id + "F15", { "sketchPlane" : qUnion([Q0])});
            skLineSegment(sketch, "E17.bottom", {"start": v(235, 0) * mm, "end": v(350, 0) * mm});
            skLineSegment(sketch, "E17.top", {"start": v(235, -120) * mm, "end": v(350, -120) * mm});
            skLineSegment(sketch, "E17.left", {"start": v(235, 0) * mm, "end": v(235, -120) * mm});
            skLineSegment(sketch, "E17.right", {"start": v(350, 0) * mm, "end": v(350, -120) * mm});
            skSolve(sketch);
        }
        {
            var Q0;
            Q0 = qSketchRegion(id + "F15", true);
            var Q1;
            Q1=makeQuery(id+"F14.boolean.opBoolean","MERGE",FACE,{"derivedFrom":[makeQuery(id+"F2.opExtrude","CAP_FACE",FACE,{"disambiguationData":[OSD([sQuery(id+"F0.wireOp",EDGE,"E0.bottom"),sQuery(id+"F0.wireOp",EDGE,"E0.top"),sQuery(id+"F0.wireOp",EDGE,"E0.left"),sQuery(id+"F0.wireOp",EDGE,"E0.right")])],"isStart":false}),makeQuery(id+"F14.opExtrude","CAP_FACE",FACE,{"disambiguationData":[OSD([sQuery(id+"F13.wireOp",EDGE,"E16.bottom"),sQuery(id+"F13.wireOp",EDGE,"E16.top"),sQuery(id+"F13.wireOp",EDGE,"E16.left"),sQuery(id+"F13.wireOp",EDGE,"E16.right")])],"isStart":false})]});
            extrude(context, id + "F16", {"entities" : qUnion([Q0]), "operationType" : NewBodyOperationType.ADD, "oppositeDirection" : true, "endBoundEntityFace" : qUnion([Q1]), "depth" : 570 * mm});
        }
    });
